SOLIDWORKS PART (.sldprt)
format: sldprt  version: not decoded by parser v0  size: 147,456 bytes
history: native  units: mm
features: sketch x4, plane x3, fillet x2, cut_extrude x2, revolve x1, thread x1, cut_revolve x1, pattern_linear x1 (+8 scaffold rows collapsed; 1 parser-record rows omitted)
feature tree (24):
  scaffold x8  (default folders/planes/origin — collapsed)
  plane  "Plane1"
  plane  "Plane2"
  plane  "Plane3"
  parser-record x1  (decoder bookkeeping rows leaked as tree rows — omitted from the tree; the rows remain in map.json)
  revolve  "Base-Revolve"  [1 undecoded]
  sketch  "BodySke"  dims[c1.Head_fillet_rad=1.016mm c1.Head_top_radius=2.54mm c1.D1=19.05mm c1.Diameter=25.4mm c1.D3=50.8mm c1.D4=22.225mm c2.D4=45.0deg c2.D5=22.225mm c2.Head_ht=10.0mm c2.Length=60.0mm c2.D8=9.525mm c3.D8=45.0deg c3.D1=9.525mm c4.D8=9.525mm c5.D8=45.0deg c5.D1=73.025mm c6.D1=45.0deg c7.D1=9.525mm c8.D1=45.0deg c8.D4=22.225mm c9.D4=45.0deg c9.Thread_min=12.7mm c10.D4=9.525mm c10.Body_ch_ang=45.0deg c10.D8=22.225mm c11.D8=45.0deg c11.D5=22.225mm c12.D5=45.0deg c13.D5=~4.490128mm c14.D5=45.0deg c14.Head_dia=50.8mm c15.D5=~8.980256mm c15.Head_ch_ang=45.0deg c15.Head_side_ht=22.86mm c15.D9=19.05mm c15.Diameter=10.0mm c15.Head_dia=38.1mm c15.Minor_dia=8.344mm c15.Advance=1.5mm c15.Thread_nom=60.0mm c15.Thread_lim=~74.083342mm c15.Thread_length=60.0mm c16.Head_dia=16.0mm]
  thread  "ThreadCosmetic"  Diameter=55.5mm Thread_length=55.5mm Thread_minor=8.344mm  [1 undecoded]
  fillet  "Fillet1"  Radius=0.4mm Head_dia=16mm
  fillet  "Fillet2"  Radius=1.5mm
  sketch  "Sketch2"  dims[c1.D1=4.0575mm c1.D2=25.4mm c2.D2=60.0deg c2.Wall_thickness=11.427mm c2.Depth=5.0mm]
  cut_revolve  "Hex-PreBroach"  Angle=360deg
  sketch  "Sketch3"  dims[c1.D1=4.0575mm c1.D2=4.0575mm c1.Hex_size=8.115mm c1.D4=~14.664697mm c2.D4=120.0deg]
  cut_extrude  "Hex"  Depth=5mm Key_eng=5mm
  sketch  "ThdSchSke"  dims[c1.Thread_minor=~1.03886mm c1.Diameter=~1.413535mm c1.Start=~0.988134mm c1.D4=~4.446753mm c1.Vee=60.0deg c2.Thread_minor=~1.03886mm c2.Start=~2.540025mm c2.D1=~0.108159mm c2.D2=~0.108159mm c3.D1=~0.216319mm c3.SideAngle=55.0deg c3.D2=~0.216319mm c3.VeeAngle=70.0deg c3.Thread_minor=8.344mm c3.Overcut=12.5mm c3.Diameter=10.0mm c3.D6=~8.326268mm c4.D1=~8.326268mm c5.D1=90.0deg c5.Start=54.0mm c6.Start=14.5mm]
  cut_extrude  "ThreadSchematic"  [1 undecoded]
  pattern_linear  "ThdSchPat"  Count1=37 Count2=1 Spacing1=1.5mm Spacing2=50mm Num_threads=37 Advance=1.5mm CopiedFlag=0
decode coverage: 10 of 12 modeling features carry decoded parameters
note: ~ marks probable driven/reference dimensions
note: 3 parameter values undecoded
note: suppression state not decoded; provenance and decode notes live in map.json
